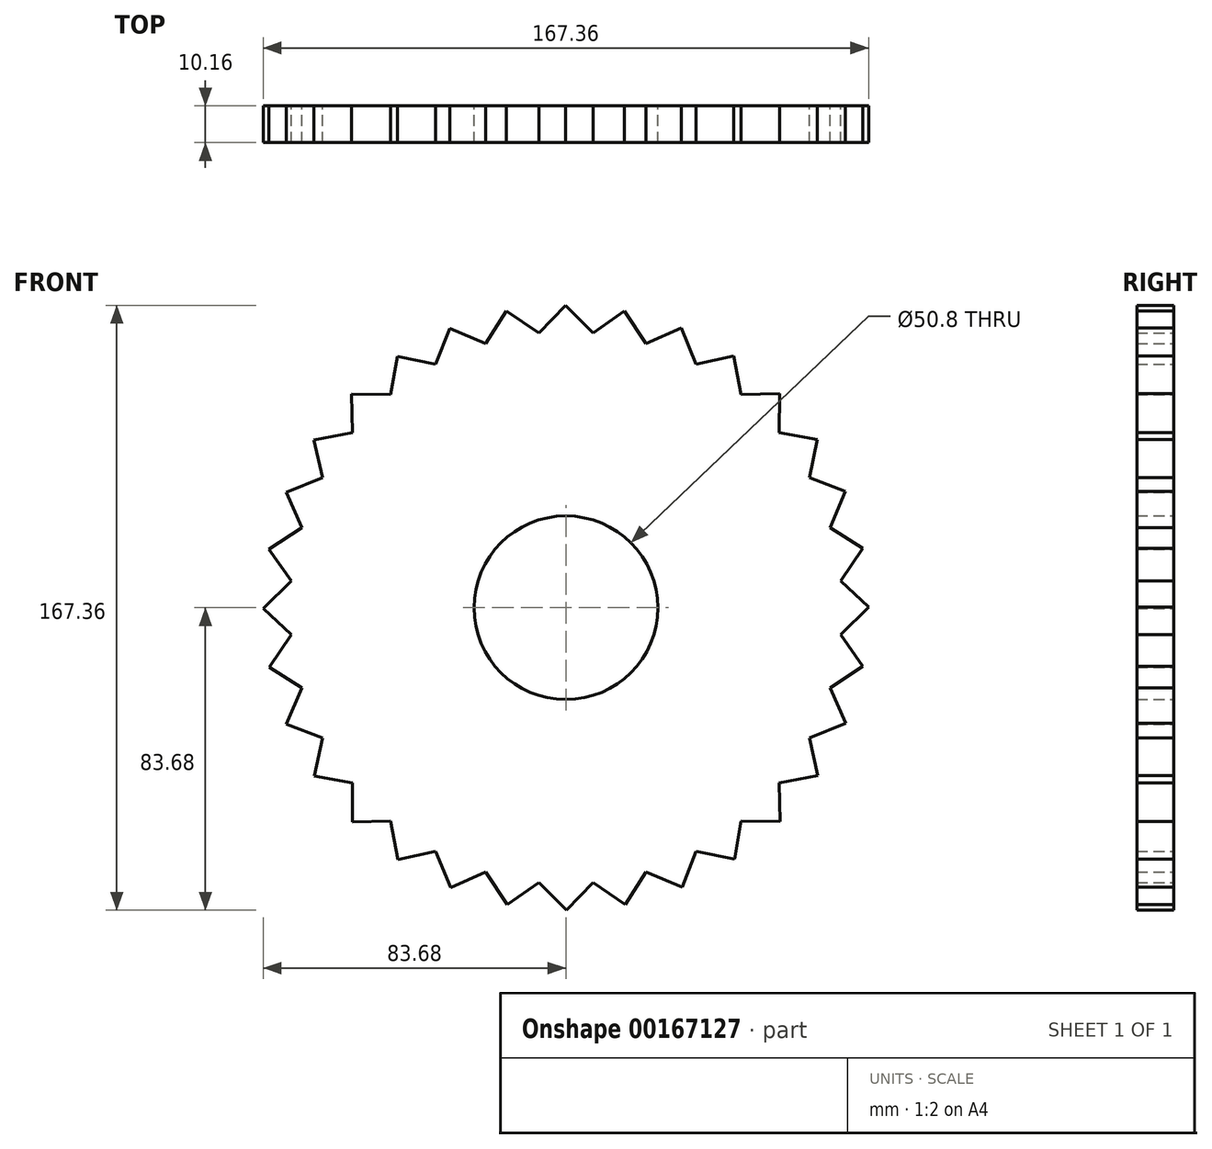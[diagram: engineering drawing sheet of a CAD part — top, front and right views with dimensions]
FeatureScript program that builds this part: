
annotation { "Feature Type Name" : "Feature", "Feature Type Description" : "" }
export const myFeature = defineFeature(function(context is Context, id is Id, definition is map)
    precondition{}
    {
        {
            var Q0;
            Q0=qCreatedBy(makeId("Front.planeOp"),FACE);
            var sketch = newSketch(context, id + "F0", { "sketchPlane" : qUnion([Q0])});
            skCircle(sketch, "E0", {"center": v(0, 0) * mm, "radius": 76.2 * mm});
            skLineSegment(sketch, "E1", {"start": v(0, 76.2) * mm, "end": v(0, 0) * mm});
            skLineSegment(sketch, "E2", {"start": v(-7.62, 75.82) * mm, "end": v(0, 83.82) * mm});
            skLineSegment(sketch, "E3", {"start": v(-0.14, 83.68) * mm, "end": v(7.62, 75.82) * mm});
            skLineSegment(sketch, "E4.1.0", {"start": v(-16.46, 82.05) * mm, "end": v(-7.32, 75.85) * mm});
            skLineSegment(sketch, "E4.1.1", {"start": v(-22.26, 72.87) * mm, "end": v(-16.35, 82.2) * mm});
            skLineSegment(sketch, "E4.2.0", {"start": v(-32.15, 77.26) * mm, "end": v(-21.97, 72.96) * mm});
            skLineSegment(sketch, "E4.2.1", {"start": v(-36.05, 67.13) * mm, "end": v(-32.08, 77.44) * mm});
            skLineSegment(sketch, "E4.3.0", {"start": v(-46.6, 69.5) * mm, "end": v(-35.79, 67.27) * mm});
            skLineSegment(sketch, "E4.3.1", {"start": v(-48.46, 58.8) * mm, "end": v(-46.57, 69.7) * mm});
            skLineSegment(sketch, "E4.4.0", {"start": v(-59.27, 59.08) * mm, "end": v(-48.22, 59) * mm});
            skLineSegment(sketch, "E4.4.1", {"start": v(-59, 48.22) * mm, "end": v(-59.27, 59.27) * mm});
            skLineSegment(sketch, "E4.5.0", {"start": v(-69.66, 46.38) * mm, "end": v(-58.8, 48.46) * mm});
            skLineSegment(sketch, "E4.5.1", {"start": v(-67.27, 35.79) * mm, "end": v(-69.7, 46.57) * mm});
            skLineSegment(sketch, "E4.6.0", {"start": v(-77.37, 31.9) * mm, "end": v(-67.13, 36.05) * mm});
            skLineSegment(sketch, "E4.6.1", {"start": v(-72.96, 21.97) * mm, "end": v(-77.44, 32.08) * mm});
            skLineSegment(sketch, "E4.7.0", {"start": v(-82.1, 16.2) * mm, "end": v(-72.87, 22.26) * mm});
            skLineSegment(sketch, "E4.7.1", {"start": v(-75.85, 7.32) * mm, "end": v(-82.2, 16.35) * mm});
            skLineSegment(sketch, "E4.8.0", {"start": v(-83.68, -0.14) * mm, "end": v(-75.82, 7.62) * mm});
            skLineSegment(sketch, "E4.8.1", {"start": v(-75.82, -7.62) * mm, "end": v(-83.82, 0) * mm});
            skLineSegment(sketch, "E4.9.0", {"start": v(-82.05, -16.46) * mm, "end": v(-75.85, -7.32) * mm});
            skLineSegment(sketch, "E4.9.1", {"start": v(-72.87, -22.26) * mm, "end": v(-82.2, -16.35) * mm});
            skLineSegment(sketch, "E4.10.0", {"start": v(-77.26, -32.15) * mm, "end": v(-72.96, -21.97) * mm});
            skLineSegment(sketch, "E4.10.1", {"start": v(-67.13, -36.05) * mm, "end": v(-77.44, -32.08) * mm});
            skLineSegment(sketch, "E4.11.0", {"start": v(-69.5, -46.6) * mm, "end": v(-67.27, -35.79) * mm});
            skLineSegment(sketch, "E4.11.1", {"start": v(-58.8, -48.46) * mm, "end": v(-69.7, -46.57) * mm});
            skLineSegment(sketch, "E4.12.0", {"start": v(-59.08, -59.27) * mm, "end": v(-59, -48.22) * mm});
            skLineSegment(sketch, "E4.12.1", {"start": v(-48.22, -59) * mm, "end": v(-59.27, -59.27) * mm});
            skLineSegment(sketch, "E4.13.0", {"start": v(-46.38, -69.66) * mm, "end": v(-48.46, -58.8) * mm});
            skLineSegment(sketch, "E4.13.1", {"start": v(-35.79, -67.27) * mm, "end": v(-46.57, -69.7) * mm});
            skLineSegment(sketch, "E4.14.0", {"start": v(-31.9, -77.37) * mm, "end": v(-36.05, -67.13) * mm});
            skLineSegment(sketch, "E4.14.1", {"start": v(-21.97, -72.96) * mm, "end": v(-32.08, -77.44) * mm});
            skLineSegment(sketch, "E4.15.0", {"start": v(-16.2, -82.1) * mm, "end": v(-22.26, -72.87) * mm});
            skLineSegment(sketch, "E4.15.1", {"start": v(-7.32, -75.85) * mm, "end": v(-16.35, -82.2) * mm});
            skLineSegment(sketch, "E4.16.0", {"start": v(0.14, -83.68) * mm, "end": v(-7.62, -75.82) * mm});
            skLineSegment(sketch, "E4.16.1", {"start": v(7.62, -75.82) * mm, "end": v(0, -83.82) * mm});
            skLineSegment(sketch, "E4.17.0", {"start": v(16.46, -82.05) * mm, "end": v(7.32, -75.85) * mm});
            skLineSegment(sketch, "E4.17.1", {"start": v(22.26, -72.87) * mm, "end": v(16.35, -82.2) * mm});
            skLineSegment(sketch, "E4.18.0", {"start": v(32.15, -77.26) * mm, "end": v(21.97, -72.96) * mm});
            skLineSegment(sketch, "E4.18.1", {"start": v(36.05, -67.13) * mm, "end": v(32.08, -77.44) * mm});
            skLineSegment(sketch, "E4.19.0", {"start": v(46.6, -69.5) * mm, "end": v(35.79, -67.27) * mm});
            skLineSegment(sketch, "E4.19.1", {"start": v(48.46, -58.8) * mm, "end": v(46.57, -69.7) * mm});
            skLineSegment(sketch, "E4.20.0", {"start": v(59.27, -59.08) * mm, "end": v(48.22, -59) * mm});
            skLineSegment(sketch, "E4.20.1", {"start": v(59, -48.22) * mm, "end": v(59.27, -59.27) * mm});
            skLineSegment(sketch, "E4.21.0", {"start": v(69.66, -46.38) * mm, "end": v(58.8, -48.46) * mm});
            skLineSegment(sketch, "E4.21.1", {"start": v(67.27, -35.79) * mm, "end": v(69.7, -46.57) * mm});
            skLineSegment(sketch, "E4.22.0", {"start": v(77.37, -31.9) * mm, "end": v(67.13, -36.05) * mm});
            skLineSegment(sketch, "E4.22.1", {"start": v(72.96, -21.97) * mm, "end": v(77.44, -32.08) * mm});
            skLineSegment(sketch, "E4.23.0", {"start": v(82.1, -16.2) * mm, "end": v(72.87, -22.26) * mm});
            skLineSegment(sketch, "E4.23.1", {"start": v(75.85, -7.32) * mm, "end": v(82.2, -16.35) * mm});
            skLineSegment(sketch, "E4.24.0", {"start": v(83.68, 0.14) * mm, "end": v(75.82, -7.62) * mm});
            skLineSegment(sketch, "E4.24.1", {"start": v(75.82, 7.62) * mm, "end": v(83.82, 0) * mm});
            skLineSegment(sketch, "E4.25.0", {"start": v(82.05, 16.46) * mm, "end": v(75.85, 7.32) * mm});
            skLineSegment(sketch, "E4.25.1", {"start": v(72.87, 22.26) * mm, "end": v(82.2, 16.35) * mm});
            skLineSegment(sketch, "E4.26.0", {"start": v(77.26, 32.15) * mm, "end": v(72.96, 21.97) * mm});
            skLineSegment(sketch, "E4.26.1", {"start": v(67.13, 36.05) * mm, "end": v(77.44, 32.08) * mm});
            skLineSegment(sketch, "E4.27.0", {"start": v(69.5, 46.6) * mm, "end": v(67.27, 35.79) * mm});
            skLineSegment(sketch, "E4.27.1", {"start": v(58.8, 48.46) * mm, "end": v(69.7, 46.57) * mm});
            skLineSegment(sketch, "E4.28.0", {"start": v(59.08, 59.27) * mm, "end": v(59, 48.22) * mm});
            skLineSegment(sketch, "E4.28.1", {"start": v(48.22, 59) * mm, "end": v(59.27, 59.27) * mm});
            skLineSegment(sketch, "E4.29.0", {"start": v(46.38, 69.66) * mm, "end": v(48.46, 58.8) * mm});
            skLineSegment(sketch, "E4.29.1", {"start": v(35.79, 67.27) * mm, "end": v(46.57, 69.7) * mm});
            skLineSegment(sketch, "E4.30.0", {"start": v(31.9, 77.37) * mm, "end": v(36.05, 67.13) * mm});
            skLineSegment(sketch, "E4.30.1", {"start": v(21.97, 72.96) * mm, "end": v(32.08, 77.44) * mm});
            skLineSegment(sketch, "E4.31.0", {"start": v(16.2, 82.1) * mm, "end": v(22.26, 72.87) * mm});
            skLineSegment(sketch, "E4.31.1", {"start": v(7.32, 75.85) * mm, "end": v(16.35, 82.2) * mm});
            skCircle(sketch, "E5", {"center": v(0, 0) * mm, "radius": 25.4 * mm});
            skSolve(sketch);
        }
        {
            var Q0;
            Q0 = qSketchRegion(id + "F0", true);
            extrude(context, id + "F1", {"entities" : qUnion([Q0]), "endBound" : BoundingType.SYMMETRIC, "depth" : 10.16 * mm});
        }
        {
            var Q0;
            {var subQ0=sQuery(id+"F0.wireOp",EDGE,"E0");var subQ39=makeQuery(id+"F0.imprint","IMPRINT",VERTEX,{"derivedFrom":subQ0});Q0=makeQuery(id+"F0.imprint","IMPRINT",FACE,{"disambiguationData":[TD([[makeQuery(id+"F0.imprint","IMPRINT",EDGE,{"disambiguationData":[TD([[subQ39,1.0]])],"derivedFrom":subQ0}),1.0]])]});}
            extrude(context, id + "F2", {"entities" : qUnion([Q0]), "operationType" : NewBodyOperationType.ADD, "endBound" : BoundingType.SYMMETRIC, "depth" : 10.16 * mm});
        }
        {
            var Q0;
            Q0=makeQuery(id+"F0.imprint","IMPRINT",FACE,{"disambiguationData":[TD([[makeQuery(id+"F0.imprint","IMPRINT",EDGE,{"derivedFrom":sQuery(id+"F0.wireOp",EDGE,"E5")}),-1.0]])]});
            extrude(context, id + "F3", {"entities" : qUnion([Q0]), "operationType" : NewBodyOperationType.ADD, "endBound" : BoundingType.SYMMETRIC, "depth" : 10.16 * mm});
        }
    });
